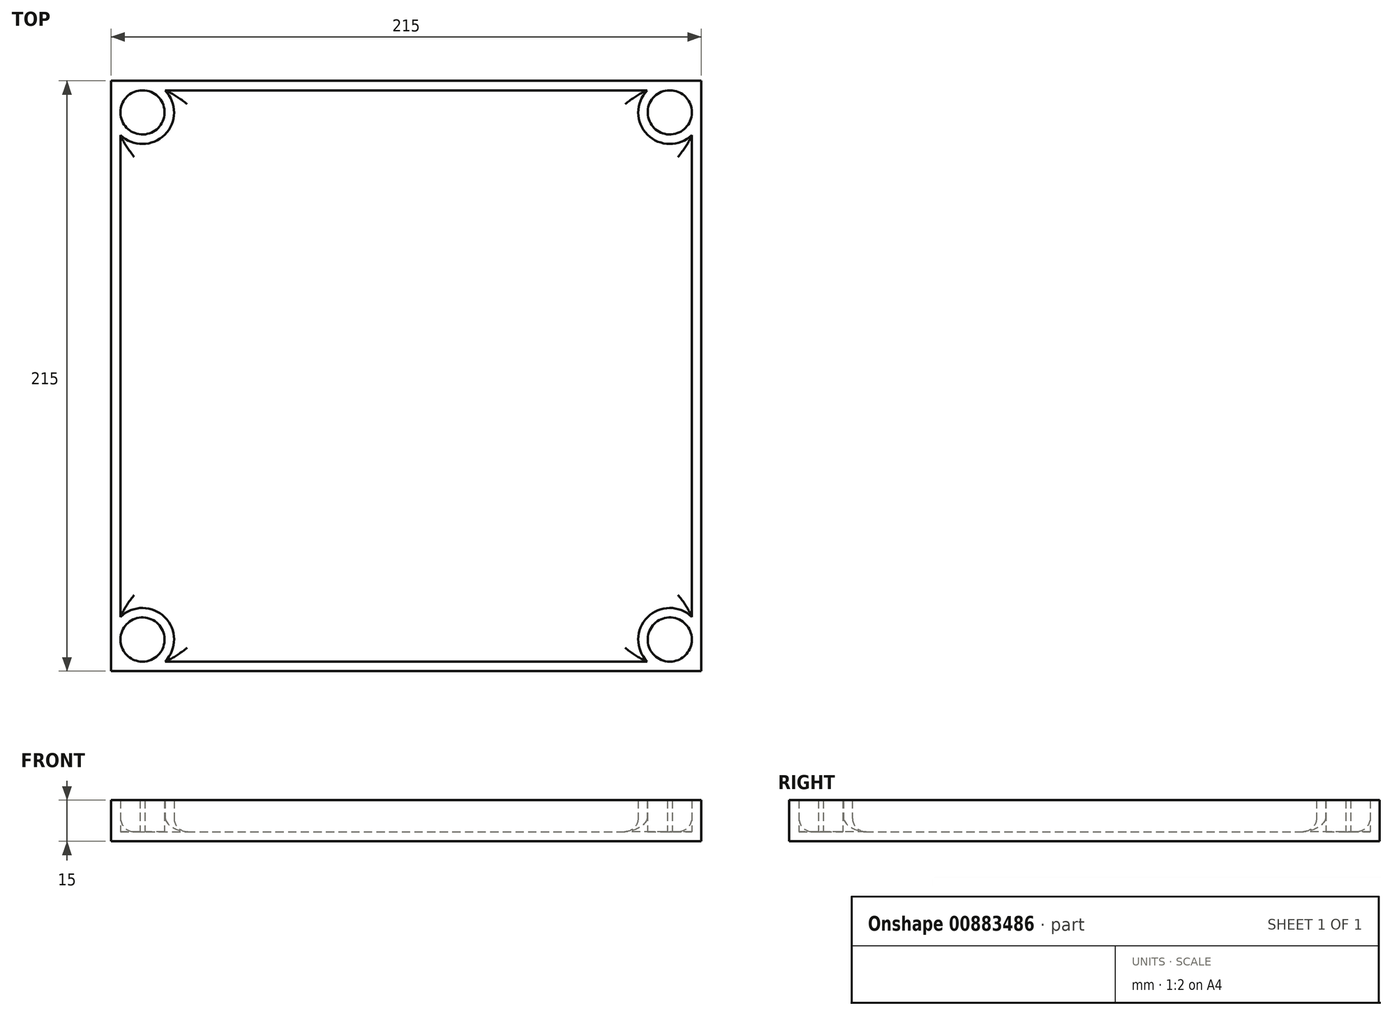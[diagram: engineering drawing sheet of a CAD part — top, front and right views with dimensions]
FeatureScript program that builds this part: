
annotation { "Feature Type Name" : "Feature", "Feature Type Description" : "" }
export const myFeature = defineFeature(function(context is Context, id is Id, definition is map)
    precondition{}
    {
        {
            var Q0;
            Q0=qCreatedBy(makeId("Top.planeOp"),FACE);
            var sketch = newSketch(context, id + "F0", { "sketchPlane" : qUnion([Q0])});
            skLineSegment(sketch, "E0.bottom", {"start": v(0, 0) * mm, "end": v(215, 0) * mm});
            skLineSegment(sketch, "E0.top", {"start": v(0, 215) * mm, "end": v(215, 215) * mm});
            skLineSegment(sketch, "E0.left", {"start": v(0, 0) * mm, "end": v(0, 215) * mm});
            skLineSegment(sketch, "E0.right", {"start": v(215, 0) * mm, "end": v(215, 215) * mm});
            skSolve(sketch);
        }
        {
            var Q0;
            Q0 = qSketchRegion(id + "F0", true);
            extrude(context, id + "F1", {"entities" : qUnion([Q0]), "depth" : 15 * mm, "offsetDistance" : 25 * mm});
        }
        {
            var Q0;
            Q0=makeQuery(id+"F1.opExtrude","CAP_FACE",FACE,{"disambiguationData":[OSD([sQuery(id+"F0.wireOp",EDGE,"E0.bottom"),sQuery(id+"F0.wireOp",EDGE,"E0.top"),sQuery(id+"F0.wireOp",EDGE,"E0.left"),sQuery(id+"F0.wireOp",EDGE,"E0.right")])],"isStart":false});
            shell(context, id + "F2", {"entities" : qUnion([Q0]), "thickness" : 3.5 * mm});
        }
        {
            var Q0;
            Q0=makeQuery(id+"F1.opExtrude","CAP_FACE",FACE,{"disambiguationData":[OSD([sQuery(id+"F0.wireOp",EDGE,"E0.bottom"),sQuery(id+"F0.wireOp",EDGE,"E0.top"),sQuery(id+"F0.wireOp",EDGE,"E0.left"),sQuery(id+"F0.wireOp",EDGE,"E0.right")])],"isStart":true});
            var sketch = newSketch(context, id + "F3", { "sketchPlane" : qUnion([Q0])});
            skLineSegment(sketch, "E1", {"start": v(0, -11.5) * mm, "end": v(11.5, -11.5) * mm, "construction": true});
            skLineSegment(sketch, "E2", {"start": v(11.5, -11.5) * mm, "end": v(11.5, 0) * mm, "construction": true});
            skCircle(sketch, "E3", {"center": v(11.5, -11.5) * mm, "radius": 8.05 * mm});
            skCircle(sketch, "E4", {"center": v(11.5, -11.5) * mm, "radius": 11.5 * mm});
            skCircle(sketch, "E5.0.1.0", {"center": v(11.5, -203.5) * mm, "radius": 8.05 * mm});
            skCircle(sketch, "E5.0.1.1", {"center": v(11.5, -203.5) * mm, "radius": 11.5 * mm});
            skCircle(sketch, "E5.1.0.0", {"center": v(203.5, -11.5) * mm, "radius": 8.05 * mm});
            skCircle(sketch, "E5.1.0.1", {"center": v(203.5, -11.5) * mm, "radius": 11.5 * mm});
            skCircle(sketch, "E5.1.1.0", {"center": v(203.5, -203.5) * mm, "radius": 8.05 * mm});
            skCircle(sketch, "E5.1.1.1", {"center": v(203.5, -203.5) * mm, "radius": 11.5 * mm});
            skSolve(sketch);
        }
        {
            var Q0;
            Q0 = qSketchRegion(id + "F3", true);
            var Q1;
            Q1=makeQuery(id+"F1.opExtrude","CAP_FACE",FACE,{"disambiguationData":[OSD([sQuery(id+"F0.wireOp",EDGE,"E0.bottom"),sQuery(id+"F0.wireOp",EDGE,"E0.top"),sQuery(id+"F0.wireOp",EDGE,"E0.left"),sQuery(id+"F0.wireOp",EDGE,"E0.right")])],"isStart":false});
            extrude(context, id + "F4", {"entities" : qUnion([Q0]), "operationType" : NewBodyOperationType.ADD, "endBound" : BoundingType.UP_TO_SURFACE, "oppositeDirection" : true, "depth" : 20 * mm, "endBoundEntityFace" : qUnion([Q1]), "offsetDistance" : 25 * mm});
        }
        {
            var Q0;
            Q0=makeQuery(id+"F4.boolean.opBoolean","INTERSECT",EDGE,{"derivedFrom":[makeQuery(id+"F2.opShell","OFFSET_FACE",FACE,{"disambiguationData":[OSD([sQuery(id+"F0.wireOp",EDGE,"E0.bottom"),sQuery(id+"F0.wireOp",EDGE,"E0.top"),sQuery(id+"F0.wireOp",EDGE,"E0.left"),sQuery(id+"F0.wireOp",EDGE,"E0.right")])]}),makeQuery(id+"F4.opExtrude","SWEPT_FACE",FACE,{"disambiguationData":[OSD([sQuery(id+"F3.wireOp",EDGE,"E5.0.1.1")])]})]});
            var Q1;
            {var subQ0=sQuery(id+"F0.wireOp",EDGE,"E0.top");Q1=makeQuery(id+"F4.boolean.opBoolean","SPLIT",EDGE,{"disambiguationData":[TD([makeQuery(id+"F4.opExtrude","SWEPT_FACE",FACE,{"disambiguationData":[OSD([sQuery(id+"F3.wireOp",EDGE,"E5.0.1.1")])]})])],"derivedFrom":makeQuery(id+"F2.opShell","OFFSET_EDGE",EDGE,{"disambiguationData":[OSD([subQ0]),TDD([makeQuery(id+"F1.opExtrude","CAP_EDGE",EDGE,{"disambiguationData":[OSD([subQ0])],"isStart":true})])]})});}
            var Q2;
            {var subQ0=sQuery(id+"F0.wireOp",EDGE,"E0.left");Q2=makeQuery(id+"F4.boolean.opBoolean","SPLIT",EDGE,{"disambiguationData":[TD([makeQuery(id+"F4.opExtrude","SWEPT_FACE",FACE,{"disambiguationData":[OSD([sQuery(id+"F3.wireOp",EDGE,"E4")])]})])],"derivedFrom":makeQuery(id+"F2.opShell","OFFSET_EDGE",EDGE,{"disambiguationData":[OSD([subQ0]),TDD([makeQuery(id+"F1.opExtrude","CAP_EDGE",EDGE,{"disambiguationData":[OSD([subQ0])],"isStart":true})])]})});}
            var Q3;
            Q3=makeQuery(id+"F4.boolean.opBoolean","INTERSECT",EDGE,{"derivedFrom":[makeQuery(id+"F2.opShell","OFFSET_FACE",FACE,{"disambiguationData":[OSD([sQuery(id+"F0.wireOp",EDGE,"E0.bottom"),sQuery(id+"F0.wireOp",EDGE,"E0.top"),sQuery(id+"F0.wireOp",EDGE,"E0.left"),sQuery(id+"F0.wireOp",EDGE,"E0.right")])]}),makeQuery(id+"F4.opExtrude","SWEPT_FACE",FACE,{"disambiguationData":[OSD([sQuery(id+"F3.wireOp",EDGE,"E5.1.1.1")])]})]});
            var Q4;
            {var subQ0=sQuery(id+"F0.wireOp",EDGE,"E0.right");Q4=makeQuery(id+"F4.boolean.opBoolean","SPLIT",EDGE,{"disambiguationData":[TD([makeQuery(id+"F4.opExtrude","SWEPT_FACE",FACE,{"disambiguationData":[OSD([sQuery(id+"F3.wireOp",EDGE,"E5.1.0.1")])]})])],"derivedFrom":makeQuery(id+"F2.opShell","OFFSET_EDGE",EDGE,{"disambiguationData":[OSD([subQ0]),TDD([makeQuery(id+"F1.opExtrude","CAP_EDGE",EDGE,{"disambiguationData":[OSD([subQ0])],"isStart":true})])]})});}
            var Q5;
            Q5=makeQuery(id+"F4.boolean.opBoolean","INTERSECT",EDGE,{"derivedFrom":[makeQuery(id+"F2.opShell","OFFSET_FACE",FACE,{"disambiguationData":[OSD([sQuery(id+"F0.wireOp",EDGE,"E0.bottom"),sQuery(id+"F0.wireOp",EDGE,"E0.top"),sQuery(id+"F0.wireOp",EDGE,"E0.left"),sQuery(id+"F0.wireOp",EDGE,"E0.right")])]}),makeQuery(id+"F4.opExtrude","SWEPT_FACE",FACE,{"disambiguationData":[OSD([sQuery(id+"F3.wireOp",EDGE,"E4")])]})]});
            var Q6;
            {var subQ0=sQuery(id+"F0.wireOp",EDGE,"E0.bottom");Q6=makeQuery(id+"F4.boolean.opBoolean","SPLIT",EDGE,{"disambiguationData":[TD([makeQuery(id+"F4.opExtrude","SWEPT_FACE",FACE,{"disambiguationData":[OSD([sQuery(id+"F3.wireOp",EDGE,"E4")])]})])],"derivedFrom":makeQuery(id+"F2.opShell","OFFSET_EDGE",EDGE,{"disambiguationData":[OSD([subQ0]),TDD([makeQuery(id+"F1.opExtrude","CAP_EDGE",EDGE,{"disambiguationData":[OSD([subQ0])],"isStart":true})])]})});}
            var Q7;
            Q7=makeQuery(id+"F4.boolean.opBoolean","INTERSECT",EDGE,{"derivedFrom":[makeQuery(id+"F2.opShell","OFFSET_FACE",FACE,{"disambiguationData":[OSD([sQuery(id+"F0.wireOp",EDGE,"E0.bottom"),sQuery(id+"F0.wireOp",EDGE,"E0.top"),sQuery(id+"F0.wireOp",EDGE,"E0.left"),sQuery(id+"F0.wireOp",EDGE,"E0.right")])]}),makeQuery(id+"F4.opExtrude","SWEPT_FACE",FACE,{"disambiguationData":[OSD([sQuery(id+"F3.wireOp",EDGE,"E5.1.0.1")])]})]});
            fillet(context, id + "F5", {"entities" : qUnion([Q0, Q1, Q2, Q3, Q4, Q5, Q6, Q7]), "radius" : 5 * mm, "tangentPropagation" : true, "allowEdgeOverflow" : false});
        }
    });
